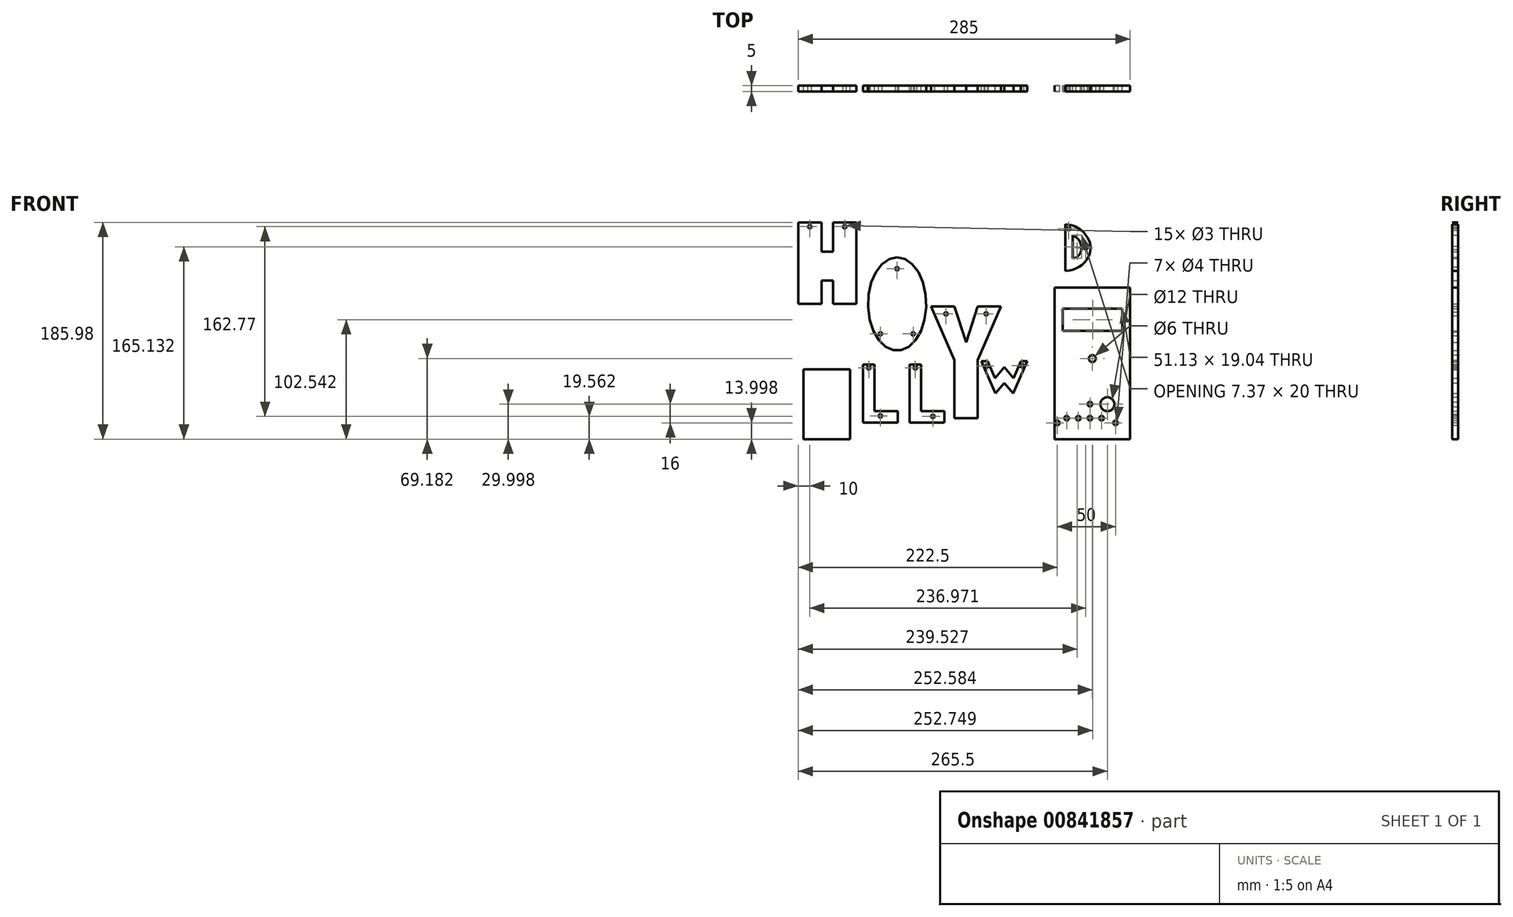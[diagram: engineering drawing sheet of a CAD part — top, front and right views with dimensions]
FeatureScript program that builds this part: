
annotation { "Feature Type Name" : "Feature", "Feature Type Description" : "" }
export const myFeature = defineFeature(function(context is Context, id is Id, definition is map)
    precondition{}
    {
        {
            var Q0;
            Q0=qCreatedBy(makeId("Front.planeOp"),FACE);
            var sketch = newSketch(context, id + "F0", { "sketchPlane" : qUnion([Q0])});
            skLineSegment(sketch, "E0.bottom", {"start": v(0, 0) * mm, "end": v(300, 0) * mm, "construction": true});
            skLineSegment(sketch, "E0.top", {"start": v(0, 200) * mm, "end": v(300, 200) * mm, "construction": true});
            skLineSegment(sketch, "E0.left", {"start": v(0, 0) * mm, "end": v(0, 200) * mm, "construction": true});
            skLineSegment(sketch, "E0.right", {"start": v(300, 0) * mm, "end": v(300, 200) * mm, "construction": true});
            skLineSegment(sketch, "E1.bottom", {"start": v(0, 200) * mm, "end": v(10, 200) * mm});
            skLineSegment(sketch, "E1.left", {"start": v(0, 200) * mm, "end": v(0, 190) * mm});
            skLineSegment(sketch, "E2", {"start": v(10, 190) * mm, "end": v(10, 120) * mm});
            skLineSegment(sketch, "E3", {"start": v(10, 120) * mm, "end": v(30, 120) * mm});
            skLineSegment(sketch, "E4", {"start": v(30, 120) * mm, "end": v(30, 140) * mm});
            skLineSegment(sketch, "E5", {"start": v(30, 140) * mm, "end": v(40, 140) * mm});
            skLineSegment(sketch, "E6", {"start": v(40, 140) * mm, "end": v(40, 120) * mm});
            skLineSegment(sketch, "E7", {"start": v(40, 120) * mm, "end": v(60, 120) * mm});
            skLineSegment(sketch, "E8", {"start": v(60, 120) * mm, "end": v(60, 190) * mm});
            skLineSegment(sketch, "E9", {"start": v(60, 190) * mm, "end": v(40, 190) * mm});
            skLineSegment(sketch, "E10", {"start": v(30, 190) * mm, "end": v(10, 190) * mm});
            skLineSegment(sketch, "E11", {"start": v(40, 190) * mm, "end": v(40, 165) * mm});
            skLineSegment(sketch, "E12", {"start": v(30, 190) * mm, "end": v(30, 165) * mm});
            skLineSegment(sketch, "E13", {"start": v(30, 165) * mm, "end": v(40, 165) * mm});
            skEllipse(sketch, "E14", {"center": v(95, 120) * mm, "majorRadius": 40 * mm, "minorRadius": 25 * mm, "majorAxis": v(0, 1)});
            skLineSegment(sketch, "E15", {"start": v(65.63, 68.08) * mm, "end": v(65.63, 18.08) * mm});
            skLineSegment(sketch, "E16", {"start": v(65.63, 18.08) * mm, "end": v(95.63, 18.08) * mm});
            skLineSegment(sketch, "E17", {"start": v(95.63, 18.08) * mm, "end": v(95.63, 28.08) * mm});
            skLineSegment(sketch, "E18", {"start": v(95.63, 28.08) * mm, "end": v(75.63, 28.08) * mm});
            skLineSegment(sketch, "E19", {"start": v(75.63, 28.08) * mm, "end": v(75.63, 68.08) * mm});
            skLineSegment(sketch, "E20", {"start": v(75.63, 68.08) * mm, "end": v(65.63, 68.08) * mm});
            skLineSegment(sketch, "E21", {"start": v(105.63, 26.2) * mm, "end": v(105.63, 68.08) * mm});
            skLineSegment(sketch, "E22", {"start": v(105.63, 68.08) * mm, "end": v(115.63, 68.08) * mm});
            skLineSegment(sketch, "E23", {"start": v(115.63, 68.08) * mm, "end": v(115.63, 28.08) * mm});
            skLineSegment(sketch, "E24", {"start": v(115.63, 28.08) * mm, "end": v(135.63, 28.08) * mm});
            skLineSegment(sketch, "E25", {"start": v(135.63, 28.08) * mm, "end": v(135.63, 18.08) * mm});
            skLineSegment(sketch, "E26", {"start": v(135.63, 18.08) * mm, "end": v(105.63, 18.08) * mm});
            skLineSegment(sketch, "E27", {"start": v(105.63, 26.2) * mm, "end": v(105.63, 18.08) * mm});
            skLineSegment(sketch, "E28", {"start": v(144.2, 22.01) * mm, "end": v(144.2, 72.01) * mm});
            skLineSegment(sketch, "E29", {"start": v(144.2, 72.01) * mm, "end": v(124.2, 117.84) * mm});
            skLineSegment(sketch, "E30", {"start": v(124.2, 117.84) * mm, "end": v(144.2, 117.84) * mm});
            skLineSegment(sketch, "E31", {"start": v(154.2, 87.01) * mm, "end": v(144.2, 117.84) * mm});
            skLineSegment(sketch, "E32", {"start": v(144.2, 22.01) * mm, "end": v(154.2, 22.01) * mm});
            skLineSegment(sketch, "E33.MirrorCS", {"start": v(164.2, 22.01) * mm, "end": v(154.2, 22.01) * mm});
            skLineSegment(sketch, "E34.MirrorCS", {"start": v(164.2, 22.01) * mm, "end": v(164.2, 72.01) * mm});
            skLineSegment(sketch, "E35.MirrorCS", {"start": v(164.2, 72.01) * mm, "end": v(184.2, 117.84) * mm});
            skLineSegment(sketch, "E36.MirrorCS", {"start": v(154.2, 87.01) * mm, "end": v(164.2, 117.84) * mm});
            skLineSegment(sketch, "E37.MirrorCS", {"start": v(184.2, 117.84) * mm, "end": v(164.2, 117.84) * mm});
            skLineSegment(sketch, "E38", {"start": v(300, 4.02) * mm, "end": v(295, 4.02) * mm});
            skLineSegment(sketch, "E39", {"start": v(295, 4.02) * mm, "end": v(230, 4.02) * mm});
            skLineSegment(sketch, "E40", {"start": v(230, 4.02) * mm, "end": v(230, 134.02) * mm});
            skLineSegment(sketch, "E41", {"start": v(230, 134.02) * mm, "end": v(295, 134.02) * mm});
            skLineSegment(sketch, "E42", {"start": v(295, 134.02) * mm, "end": v(295, 4.02) * mm});
            skLineSegment(sketch, "E43", {"start": v(239.32, 188.53) * mm, "end": v(239.32, 148.53) * mm});
            skFitSpline(sketch, "E44", {"points": [v(239.32, 148.53) * mm, v(261.12, 168.42) * mm, v(239.32, 188.53) * mm], "startDerivative": vector(76.84, 1.15) * mm, "endDerivative": vector(-71.24, 3.83) * mm});
            skLineSegment(sketch, "E45", {"start": v(245.84, 179.15) * mm, "end": v(245.84, 159.15) * mm});
            skFitSpline(sketch, "E46", {"points": [v(245.84, 159.15) * mm, v(253.22, 168.16) * mm, v(245.84, 179.15) * mm], "startDerivative": vector(34.53, 6.1) * mm, "endDerivative": vector(-31.44, 17.2) * mm});
            skLineSegment(sketch, "E47", {"start": v(237.18, 116.08) * mm, "end": v(237.18, 97.04) * mm});
            skLineSegment(sketch, "E48", {"start": v(237.18, 116.08) * mm, "end": v(288.31, 116.08) * mm});
            skLineSegment(sketch, "E49", {"start": v(288.31, 116.08) * mm, "end": v(288.31, 97.04) * mm});
            skLineSegment(sketch, "E50", {"start": v(288.31, 97.04) * mm, "end": v(237.18, 97.04) * mm});
            skLineSegment(sketch, "E51", {"start": v(232.5, 18.02) * mm, "end": v(232.5, 22.02) * mm});
            skLineSegment(sketch, "E52", {"start": v(232.5, 22.02) * mm, "end": v(240.5, 22.02) * mm});
            skCircle(sketch, "E53", {"center": v(240.5, 22.02) * mm, "radius": 2 * mm});
            skLineSegment(sketch, "E54", {"start": v(240.5, 22.02) * mm, "end": v(250.5, 22.02) * mm});
            skCircle(sketch, "E55", {"center": v(250.5, 22.02) * mm, "radius": 2 * mm});
            skLineSegment(sketch, "E56", {"start": v(250.5, 22.02) * mm, "end": v(260.5, 22.02) * mm});
            skCircle(sketch, "E57", {"center": v(260.5, 22.02) * mm, "radius": 2 * mm});
            skLineSegment(sketch, "E58", {"start": v(260.5, 22.02) * mm, "end": v(270.5, 22.02) * mm});
            skCircle(sketch, "E59", {"center": v(270.5, 22.02) * mm, "radius": 2 * mm});
            skCircle(sketch, "E60", {"center": v(260.5, 34.02) * mm, "radius": 2 * mm});
            skLineSegment(sketch, "E61", {"start": v(260.5, 34.02) * mm, "end": v(275.5, 34.02) * mm});
            skCircle(sketch, "E62", {"center": v(275.5, 34.02) * mm, "radius": 6 * mm});
            skLineSegment(sketch, "E63", {"start": v(270.5, 22.02) * mm, "end": v(275.5, 34.02) * mm});
            skLineSegment(sketch, "E64", {"start": v(54.69, 4.02) * mm, "end": v(54.69, 64.02) * mm});
            skLineSegment(sketch, "E65", {"start": v(54.69, 64.02) * mm, "end": v(14.69, 64.02) * mm});
            skLineSegment(sketch, "E66", {"start": v(14.69, 64.02) * mm, "end": v(14.69, 4.02) * mm});
            skLineSegment(sketch, "E67", {"start": v(14.69, 4.02) * mm, "end": v(54.69, 4.02) * mm});
            skLineSegment(sketch, "E68", {"start": v(270.5, 22.02) * mm, "end": v(282.5, 22.02) * mm});
            skLineSegment(sketch, "E69", {"start": v(282.5, 22.02) * mm, "end": v(282.5, 18.02) * mm});
            skCircle(sketch, "E70", {"center": v(282.5, 18.02) * mm, "radius": 2 * mm});
            skCircle(sketch, "E71", {"center": v(232.5, 18.02) * mm, "radius": 2 * mm});
            skCircle(sketch, "E72", {"center": v(262.58, 73.2) * mm, "radius": 3 * mm});
            skLineSegment(sketch, "E73", {"start": v(167.42, 70.95) * mm, "end": v(179.38, 43.2) * mm});
            skLineSegment(sketch, "E74", {"start": v(179.38, 43.2) * mm, "end": v(187.05, 52.2) * mm});
            skLineSegment(sketch, "E75", {"start": v(167.42, 70.95) * mm, "end": v(172.81, 70.95) * mm});
            skLineSegment(sketch, "E76", {"start": v(172.81, 70.95) * mm, "end": v(179.05, 56.46) * mm});
            skLineSegment(sketch, "E77", {"start": v(179.05, 56.46) * mm, "end": v(187.05, 65.83) * mm});
            skLineSegment(sketch, "E78.MirrorCS", {"start": v(195.05, 56.46) * mm, "end": v(187.05, 65.83) * mm});
            skLineSegment(sketch, "E79.MirrorCS", {"start": v(194.73, 43.2) * mm, "end": v(187.05, 52.2) * mm});
            skLineSegment(sketch, "E80.MirrorCS", {"start": v(206.68, 70.95) * mm, "end": v(194.73, 43.2) * mm});
            skLineSegment(sketch, "E81.MirrorCS", {"start": v(201.3, 70.95) * mm, "end": v(195.05, 56.46) * mm});
            skLineSegment(sketch, "E82.MirrorCS", {"start": v(206.68, 70.95) * mm, "end": v(201.3, 70.95) * mm});
            skLineSegment(sketch, "E83", {"start": v(20, 190) * mm, "end": v(20, 186.35) * mm});
            skCircle(sketch, "E84", {"center": v(20, 186.35) * mm, "radius": 1.5 * mm});
            skCircle(sketch, "E85", {"center": v(50, 186.35) * mm, "radius": 1.5 * mm});
            skPoint(sketch, "E85.centerSnap0", {"position": v(50, 185.3) * mm});
            skCircle(sketch, "E86", {"center": v(95, 150.32) * mm, "radius": 1.5 * mm});
            skCircle(sketch, "E87", {"center": v(136.95, 111.54) * mm, "radius": 1.5 * mm});
            skCircle(sketch, "E88", {"center": v(171.45, 111.54) * mm, "radius": 1.5 * mm});
            skCircle(sketch, "E89", {"center": v(70.63, 65.18) * mm, "radius": 1.5 * mm});
            skPoint(sketch, "E89.centerSnap0", {"position": v(70.63, 68.08) * mm});
            skCircle(sketch, "E90", {"center": v(110.63, 65.18) * mm, "radius": 1.5 * mm});
            skPoint(sketch, "E90.centerSnap0", {"position": v(110.63, 68.08) * mm});
            skCircle(sketch, "E91", {"center": v(80.63, 23.98) * mm, "radius": 1.5 * mm});
            skPoint(sketch, "E91.centerSnap0", {"position": v(80.63, 18.08) * mm});
            skCircle(sketch, "E92", {"center": v(171.94, 66.71) * mm, "radius": 1.5 * mm});
            skCircle(sketch, "E93", {"center": v(202.26, 66.99) * mm, "radius": 1.5 * mm});
            skCircle(sketch, "E94", {"center": v(80.63, 94.42) * mm, "radius": 1.5 * mm});
            skCircle(sketch, "E95", {"center": v(125.63, 23.58) * mm, "radius": 1.5 * mm});
            skPoint(sketch, "E95.centerSnap0", {"position": v(125.63, 28.08) * mm});
            skCircle(sketch, "E96", {"center": v(108.74, 94.42) * mm, "radius": 1.5 * mm});
            skCircle(sketch, "E97", {"center": v(242.3, 184.74) * mm, "radius": 1.5 * mm});
            skCircle(sketch, "E98", {"center": v(256.97, 168.19) * mm, "radius": 1.5 * mm});
            skSolve(sketch);
        }
        {
            var Q0;
            {var subQ1=sQuery(id+"F0.wireOp",EDGE,"E2");Q0=makeQuery(id+"F0.imprint","IMPRINT",FACE,{"disambiguationData":[TD([[makeQuery(id+"F0.imprint","IMPRINT",EDGE,{"derivedFrom":subQ1}),1.0]])]});}
            extrude(context, id + "F1", {"entities" : qUnion([Q0]), "depth" : 5 * mm, "offsetDistance" : 25 * mm});
        }
        {
            var Q0;
            Q0=makeQuery(id+"F0.imprint","IMPRINT",FACE,{"disambiguationData":[TD([[makeQuery(id+"F0.imprint","IMPRINT",EDGE,{"derivedFrom":sQuery(id+"F0.wireOp",EDGE,"E14")}),1.0]])]});
            extrude(context, id + "F2", {"entities" : qUnion([Q0]), "depth" : 5 * mm, "offsetDistance" : 25 * mm});
        }
        {
            var Q0;
            Q0=makeQuery(id+"F0.imprint","IMPRINT",FACE,{"disambiguationData":[TD([[makeQuery(id+"F0.imprint","IMPRINT",EDGE,{"derivedFrom":sQuery(id+"F0.wireOp",EDGE,"E64")}),1.0]])]});
            extrude(context, id + "F3", {"entities" : qUnion([Q0]), "depth" : 5 * mm, "offsetDistance" : 25 * mm});
        }
        {
            var Q0;
            Q0=makeQuery(id+"F0.imprint","IMPRINT",FACE,{"disambiguationData":[TD([[makeQuery(id+"F0.imprint","IMPRINT",EDGE,{"derivedFrom":sQuery(id+"F0.wireOp",EDGE,"E15")}),1.0]])]});
            extrude(context, id + "F4", {"entities" : qUnion([Q0]), "depth" : 5 * mm, "offsetDistance" : 25 * mm});
        }
        {
            var Q0;
            Q0=makeQuery(id+"F0.imprint","IMPRINT",FACE,{"disambiguationData":[TD([[makeQuery(id+"F0.imprint","IMPRINT",EDGE,{"derivedFrom":sQuery(id+"F0.wireOp",EDGE,"E21")}),-1.0]])]});
            extrude(context, id + "F5", {"entities" : qUnion([Q0]), "depth" : 5 * mm, "offsetDistance" : 25 * mm});
        }
        {
            var Q0;
            Q0=makeQuery(id+"F0.imprint","IMPRINT",FACE,{"disambiguationData":[TD([[makeQuery(id+"F0.imprint","IMPRINT",EDGE,{"derivedFrom":sQuery(id+"F0.wireOp",EDGE,"E28")}),-1.0]])]});
            extrude(context, id + "F6", {"entities" : qUnion([Q0]), "depth" : 5 * mm, "offsetDistance" : 25 * mm});
        }
        {
            var Q0;
            Q0=makeQuery(id+"F0.imprint","IMPRINT",FACE,{"disambiguationData":[TD([[makeQuery(id+"F0.imprint","IMPRINT",EDGE,{"derivedFrom":sQuery(id+"F0.wireOp",EDGE,"E73")}),1.0]])]});
            extrude(context, id + "F7", {"entities" : qUnion([Q0]), "depth" : 5 * mm, "offsetDistance" : 25 * mm});
        }
        {
            var Q0;
            Q0=makeQuery(id+"F0.imprint","IMPRINT",FACE,{"disambiguationData":[TD([[makeQuery(id+"F0.imprint","IMPRINT",EDGE,{"derivedFrom":sQuery(id+"F0.wireOp",EDGE,"E39")}),-1.0]])]});
            extrude(context, id + "F8", {"entities" : qUnion([Q0]), "depth" : 5 * mm, "offsetDistance" : 25 * mm});
        }
        {
            var Q0;
            Q0=makeQuery(id+"F0.imprint","IMPRINT",FACE,{"disambiguationData":[TD([[makeQuery(id+"F0.imprint","IMPRINT",EDGE,{"derivedFrom":sQuery(id+"F0.wireOp",EDGE,"E43")}),1.0]])]});
            extrude(context, id + "F9", {"entities" : qUnion([Q0]), "depth" : 5 * mm, "offsetDistance" : 25 * mm});
        }
    });
